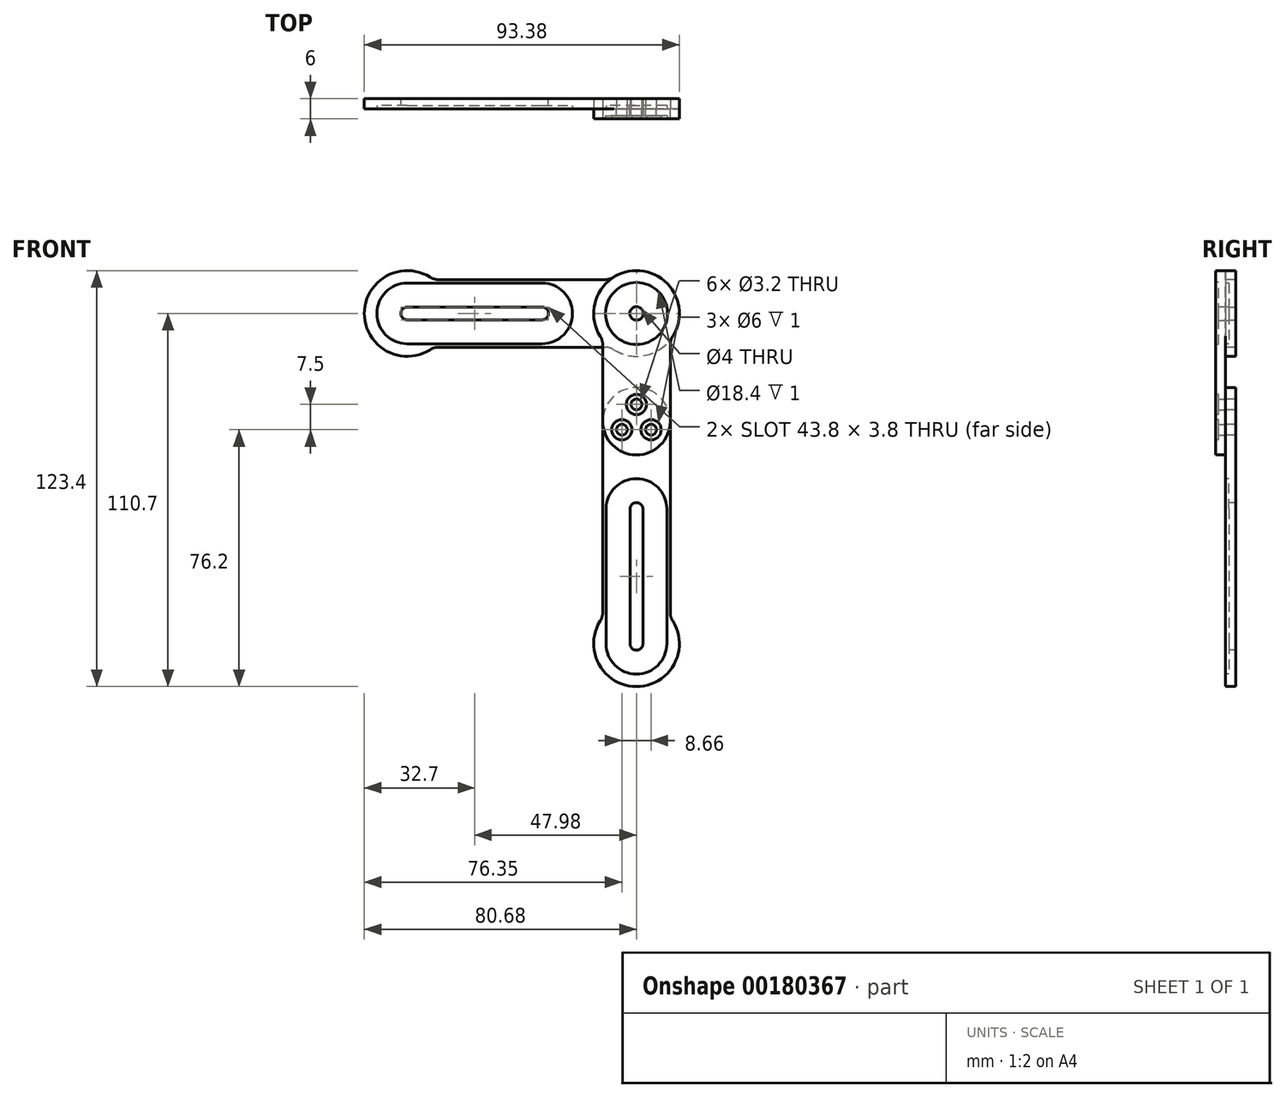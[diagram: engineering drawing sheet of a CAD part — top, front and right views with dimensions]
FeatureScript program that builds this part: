
annotation { "Feature Type Name" : "Feature", "Feature Type Description" : "" }
export const myFeature = defineFeature(function(context is Context, id is Id, definition is map)
    precondition{}
    {
        {
            var Q0;
            Q0=qCreatedBy(makeId("Front.planeOp"),FACE);
            var sketch = newSketch(context, id + "F0", { "sketchPlane" : qUnion([Q0])});
            skLineSegment(sketch, "E0.bottom", {"start": v(0, 0) * mm, "end": v(67.98, 0) * mm, "construction": true});
            skLineSegment(sketch, "E0.top", {"start": v(0, 20) * mm, "end": v(67.98, 20) * mm, "construction": true});
            skLineSegment(sketch, "E0.left", {"start": v(0, 0) * mm, "end": v(0, 20) * mm, "construction": true});
            skLineSegment(sketch, "E0.right", {"start": v(67.98, 0) * mm, "end": v(67.98, 20) * mm, "construction": true});
            skArc(sketch, "E1", {"start": v(0, 0) * mm, "mid": v(-10, 10) * mm, "end": v(0, 20) * mm, "construction": true});
            skArc(sketch, "E2", {"start": v(67.98, 20) * mm, "mid": v(77.98, 10) * mm, "end": v(67.98, 0) * mm, "construction": true});
            skCircle(sketch, "E3", {"center": v(67.98, 10) * mm, "radius": 2 * mm});
            skLineSegment(sketch, "E4", {"start": v(0, 10) * mm, "end": v(20, 10) * mm, "construction": true});
            skLineSegment(sketch, "E5.bottom", {"start": v(0, 11.9) * mm, "end": v(40, 11.9) * mm});
            skLineSegment(sketch, "E5.top", {"start": v(0, 8.1) * mm, "end": v(40, 8.1) * mm});
            skLineSegment(sketch, "E5.left", {"start": v(0, 11.9) * mm, "end": v(0, 8.1) * mm, "construction": true});
            skLineSegment(sketch, "E5.right", {"start": v(40, 11.9) * mm, "end": v(40, 8.1) * mm, "construction": true});
            skPoint(sketch, "E5.middle", {"position": v(20, 10) * mm});
            skArc(sketch, "E6", {"start": v(0, 8.1) * mm, "mid": v(-1.9, 10) * mm, "end": v(0, 11.9) * mm});
            skArc(sketch, "E7", {"start": v(40, 8.1) * mm, "mid": v(41.9, 10) * mm, "end": v(40, 11.9) * mm});
            skCircle(sketch, "E8", {"center": v(67.98, 10) * mm, "radius": 12.7 * mm, "construction": true});
            skCircle(sketch, "E9", {"center": v(0, 10) * mm, "radius": 12.7 * mm, "construction": true});
            skLineSegment(sketch, "E10", {"start": v(60.15, 20) * mm, "end": v(7.83, 20) * mm});
            skLineSegment(sketch, "E11", {"start": v(7.83, 0) * mm, "end": v(60.15, 0) * mm});
            skArc(sketch, "E12", {"start": v(7.83, 20) * mm, "mid": v(-12.7, 10) * mm, "end": v(7.83, 0) * mm});
            skArc(sketch, "E13", {"start": v(60.15, 20) * mm, "mid": v(80.68, 10) * mm, "end": v(60.15, 0) * mm});
            skSolve(sketch);
        }
        {
            var Q0;
            Q0 = qSketchRegion(id + "F0", true);
            extrude(context, id + "F1", {"entities" : qUnion([Q0]), "depth" : 3 * mm, "offsetDistance" : 25 * mm});
        }
        {
            var Q0;
            Q0=makeQuery(id+"F1.opExtrude","CAP_FACE",FACE,{"disambiguationData":[OSD([sQuery(id+"F0.wireOp",EDGE,"E0.bottom"),sQuery(id+"F0.wireOp",EDGE,"E0.top"),sQuery(id+"F0.wireOp",EDGE,"E1"),sQuery(id+"F0.wireOp",EDGE,"E2"),sQuery(id+"F0.wireOp",EDGE,"E3"),sQuery(id+"F0.wireOp",EDGE,"E5.bottom"),sQuery(id+"F0.wireOp",EDGE,"E5.top"),sQuery(id+"F0.wireOp",EDGE,"E6"),sQuery(id+"F0.wireOp",EDGE,"E7")])],"isStart":false});
            var sketch = newSketch(context, id + "F2", { "sketchPlane" : qUnion([Q0])});
            skLineSegment(sketch, "E14", {"start": v(0, 10) * mm, "end": v(40, 10) * mm, "construction": true});
            skLineSegment(sketch, "E15.bottom", {"start": v(40, 19) * mm, "end": v(0, 19) * mm});
            skLineSegment(sketch, "E15.top", {"start": v(40, 1) * mm, "end": v(0, 1) * mm});
            skLineSegment(sketch, "E15.left", {"start": v(40, 19) * mm, "end": v(40, 1) * mm, "construction": true});
            skLineSegment(sketch, "E15.right", {"start": v(0, 19) * mm, "end": v(0, 1) * mm, "construction": true});
            skPoint(sketch, "E15.middle", {"position": v(20, 10) * mm});
            skArc(sketch, "E16", {"start": v(0, 1) * mm, "mid": v(-9, 10) * mm, "end": v(0, 19) * mm});
            skArc(sketch, "E17", {"start": v(40, 19) * mm, "mid": v(49, 10) * mm, "end": v(40, 1) * mm});
            skCircle(sketch, "E18", {"center": v(67.98, 10) * mm, "radius": 9 * mm});
            skSolve(sketch);
        }
        {
            var Q0;
            Q0=makeQuery(id+"F2.imprint","IMPRINT",FACE,{"disambiguationData":[TD([[makeQuery(id+"F2.imprint","IMPRINT",EDGE,{"derivedFrom":sQuery(id+"F2.wireOp",EDGE,"E15.bottom")}),1.0]])]});
            extrude(context, id + "F3", {"entities" : qUnion([Q0]), "operationType" : NewBodyOperationType.REMOVE, "oppositeDirection" : true, "depth" : 1 * mm, "offsetDistance" : 25 * mm});
        }
        {
            var Q0;
            Q0=makeQuery(id+"F1.opExtrude","CAP_FACE",FACE,{"disambiguationData":[OSD([sQuery(id+"F0.wireOp",EDGE,"E0.bottom"),sQuery(id+"F0.wireOp",EDGE,"E0.top"),sQuery(id+"F0.wireOp",EDGE,"E1"),sQuery(id+"F0.wireOp",EDGE,"E2"),sQuery(id+"F0.wireOp",EDGE,"E3"),sQuery(id+"F0.wireOp",EDGE,"E5.bottom"),sQuery(id+"F0.wireOp",EDGE,"E5.top"),sQuery(id+"F0.wireOp",EDGE,"E6"),sQuery(id+"F0.wireOp",EDGE,"E7")])],"isStart":false});
            var sketch = newSketch(context, id + "F4", { "sketchPlane" : qUnion([Q0])});
            skLineSegment(sketch, "E19", {"start": v(67.98, 10) * mm, "end": v(67.98, -22) * mm, "construction": true});
            skLineSegment(sketch, "E20.top", {"start": v(77.98, -22) * mm, "end": v(57.98, -22) * mm, "construction": true});
            skLineSegment(sketch, "E20.left", {"start": v(77.98, 2.17) * mm, "end": v(77.98, -22) * mm});
            skLineSegment(sketch, "E20.right", {"start": v(57.98, 2.17) * mm, "end": v(57.98, -22) * mm});
            skPoint(sketch, "E20.middle", {"position": v(67.98, -6) * mm});
            skPoint(sketch, "E20.cornerSnap0", {"position": v(67.98, 10) * mm});
            skArc(sketch, "E21", {"start": v(77.98, -22) * mm, "mid": v(67.98, -32) * mm, "end": v(57.98, -22) * mm});
            skCircle(sketch, "E22", {"center": v(67.98, 10) * mm, "radius": 2 * mm});
            skCircle(sketch, "E23", {"center": v(67.98, -17) * mm, "radius": 1.6 * mm});
            skCircle(sketch, "E24.1.0", {"center": v(63.65, -24.5) * mm, "radius": 1.6 * mm});
            skCircle(sketch, "E24.2.0", {"center": v(72.31, -24.5) * mm, "radius": 1.6 * mm});
            skCircle(sketch, "E25", {"center": v(67.98, 10) * mm, "radius": 12.7 * mm, "construction": true});
            skArc(sketch, "E26", {"start": v(57.98, 2.17) * mm, "mid": v(67.98, 22.7) * mm, "end": v(77.98, 2.17) * mm});
            skSolve(sketch);
        }
        {
            var Q0;
            Q0 = qSketchRegion(id + "F4", true);
            extrude(context, id + "F5", {"entities" : qUnion([Q0]), "depth" : 3 * mm, "offsetDistance" : 25 * mm});
        }
        {
            var Q0;
            Q0=makeQuery(id+"F5.opExtrude","CAP_FACE",FACE,{"disambiguationData":[OSD([sQuery(id+"F4.wireOp",EDGE,"E20.left"),sQuery(id+"F4.wireOp",EDGE,"E20.right"),sQuery(id+"F4.wireOp",EDGE,"CmDcXUsG-X9iP-GJQO-635Y-WhZAeqbdNLiT"),sQuery(id+"F4.wireOp",EDGE,"E21"),sQuery(id+"F4.wireOp",EDGE,"E22"),sQuery(id+"F4.wireOp",EDGE,"E23"),sQuery(id+"F4.wireOp",EDGE,"E24.1.0"),sQuery(id+"F4.wireOp",EDGE,"E24.2.0")])],"isStart":false});
            var sketch = newSketch(context, id + "F6", { "sketchPlane" : qUnion([Q0])});
            skCircle(sketch, "E27", {"center": v(67.98, -17) * mm, "radius": 3 * mm});
            skCircle(sketch, "E28", {"center": v(63.65, -24.5) * mm, "radius": 3 * mm});
            skCircle(sketch, "E29", {"center": v(72.31, -24.5) * mm, "radius": 3 * mm});
            skCircle(sketch, "E30", {"center": v(67.98, 10) * mm, "radius": 9.2 * mm});
            skSolve(sketch);
        }
        {
            var Q0;
            Q0 = qSketchRegion(id + "F6", true);
            extrude(context, id + "F7", {"entities" : qUnion([Q0]), "operationType" : NewBodyOperationType.REMOVE, "oppositeDirection" : true, "depth" : 1 * mm, "offsetDistance" : 25 * mm});
        }
        {
            var Q0;
            Q0=makeQuery(id+"F5.opExtrude","CAP_FACE",FACE,{"disambiguationData":[OSD([sQuery(id+"F4.wireOp",EDGE,"E20.left"),sQuery(id+"F4.wireOp",EDGE,"E20.right"),sQuery(id+"F4.wireOp",EDGE,"CmDcXUsG-X9iP-GJQO-635Y-WhZAeqbdNLiT"),sQuery(id+"F4.wireOp",EDGE,"E21"),sQuery(id+"F4.wireOp",EDGE,"E22"),sQuery(id+"F4.wireOp",EDGE,"E23"),sQuery(id+"F4.wireOp",EDGE,"E24.1.0"),sQuery(id+"F4.wireOp",EDGE,"E24.2.0")])],"isStart":true});
            var sketch = newSketch(context, id + "F8", { "sketchPlane" : qUnion([Q0])});
            skLineSegment(sketch, "E31", {"start": v(-67.98, -22) * mm, "end": v(-67.98, -88) * mm, "construction": true});
            skLineSegment(sketch, "E32.bottom", {"start": v(-57.98, -22) * mm, "end": v(-77.98, -22) * mm, "construction": true});
            skLineSegment(sketch, "E32.top", {"start": v(-57.98, -88) * mm, "end": v(-77.98, -88) * mm, "construction": true});
            skLineSegment(sketch, "E32.left", {"start": v(-57.98, -22) * mm, "end": v(-57.98, -88) * mm, "construction": true});
            skLineSegment(sketch, "E32.right", {"start": v(-77.98, -22) * mm, "end": v(-77.98, -88) * mm, "construction": true});
            skPoint(sketch, "E32.middle", {"position": v(-67.98, -55) * mm});
            skArc(sketch, "E33", {"start": v(-77.98, -22) * mm, "mid": v(-67.98, -12) * mm, "end": v(-57.98, -22) * mm});
            skArc(sketch, "E34", {"start": v(-57.98, -88) * mm, "mid": v(-67.98, -98) * mm, "end": v(-77.98, -88) * mm, "construction": true});
            skCircle(sketch, "E35.0", {"center": v(-63.65, -24.5) * mm, "radius": 1.6 * mm});
            skCircle(sketch, "E35.1", {"center": v(-67.98, -17) * mm, "radius": 1.6 * mm});
            skCircle(sketch, "E35.2", {"center": v(-72.31, -24.5) * mm, "radius": 1.6 * mm});
            skLineSegment(sketch, "E36", {"start": v(-67.98, -88) * mm, "end": v(-67.98, -68) * mm, "construction": true});
            skLineSegment(sketch, "E37.bottom", {"start": v(-66.08, -88) * mm, "end": v(-69.88, -88) * mm, "construction": true});
            skLineSegment(sketch, "E37.top", {"start": v(-66.08, -48) * mm, "end": v(-69.88, -48) * mm, "construction": true});
            skLineSegment(sketch, "E37.left", {"start": v(-66.08, -88) * mm, "end": v(-66.08, -48) * mm});
            skLineSegment(sketch, "E37.right", {"start": v(-69.88, -88) * mm, "end": v(-69.88, -48) * mm});
            skPoint(sketch, "E37.middle", {"position": v(-67.98, -68) * mm});
            skArc(sketch, "E38", {"start": v(-66.08, -88) * mm, "mid": v(-67.98, -89.9) * mm, "end": v(-69.88, -88) * mm});
            skArc(sketch, "E39", {"start": v(-66.08, -48) * mm, "mid": v(-67.98, -46.1) * mm, "end": v(-69.88, -48) * mm});
            skCircle(sketch, "E40", {"center": v(-67.98, -88) * mm, "radius": 12.7 * mm, "construction": true});
            skLineSegment(sketch, "E41", {"start": v(-77.98, -22) * mm, "end": v(-77.98, -80.17) * mm});
            skLineSegment(sketch, "E42", {"start": v(-57.98, -22) * mm, "end": v(-57.98, -80.17) * mm});
            skArc(sketch, "E43", {"start": v(-57.98, -80.17) * mm, "mid": v(-67.98, -100.7) * mm, "end": v(-77.98, -80.17) * mm});
            skSolve(sketch);
        }
        {
            var Q0;
            Q0 = qSketchRegion(id + "F8", true);
            extrude(context, id + "F9", {"entities" : qUnion([Q0]), "depth" : 3 * mm, "offsetDistance" : 25 * mm});
        }
        {
            var Q0;
            Q0=makeQuery(id+"F9.opExtrude","CAP_FACE",FACE,{"disambiguationData":[OSD([sQuery(id+"F8.wireOp",EDGE,"E32.left"),sQuery(id+"F8.wireOp",EDGE,"E32.right"),sQuery(id+"F8.wireOp",EDGE,"E33"),sQuery(id+"F8.wireOp",EDGE,"E34"),sQuery(id+"F8.wireOp",EDGE,"E35.0"),sQuery(id+"F8.wireOp",EDGE,"E35.1"),sQuery(id+"F8.wireOp",EDGE,"E35.2"),sQuery(id+"F8.wireOp",EDGE,"E37.left"),sQuery(id+"F8.wireOp",EDGE,"E37.right"),sQuery(id+"F8.wireOp",EDGE,"E38"),sQuery(id+"F8.wireOp",EDGE,"E39")])],"isStart":true});
            var sketch = newSketch(context, id + "F10", { "sketchPlane" : qUnion([Q0])});
            skLineSegment(sketch, "E44", {"start": v(67.98, -88) * mm, "end": v(67.98, -48) * mm, "construction": true});
            skLineSegment(sketch, "E45.bottom", {"start": v(76.98, -48) * mm, "end": v(58.98, -48) * mm, "construction": true});
            skLineSegment(sketch, "E45.top", {"start": v(76.98, -88) * mm, "end": v(58.98, -88) * mm, "construction": true});
            skLineSegment(sketch, "E45.left", {"start": v(76.98, -48) * mm, "end": v(76.98, -88) * mm});
            skLineSegment(sketch, "E45.right", {"start": v(58.98, -48) * mm, "end": v(58.98, -88) * mm});
            skPoint(sketch, "E45.middle", {"position": v(67.98, -68) * mm});
            skArc(sketch, "E46", {"start": v(58.98, -48) * mm, "mid": v(67.98, -39) * mm, "end": v(76.98, -48) * mm});
            skArc(sketch, "E47", {"start": v(76.98, -88) * mm, "mid": v(67.98, -97) * mm, "end": v(58.98, -88) * mm});
            skLineSegment(sketch, "E48", {"start": v(69.88, -88) * mm, "end": v(66.08, -88) * mm, "construction": true});
            skSolve(sketch);
        }
        {
            var Q0;
            Q0 = qSketchRegion(id + "F10", true);
            extrude(context, id + "F11", {"entities" : qUnion([Q0]), "operationType" : NewBodyOperationType.REMOVE, "oppositeDirection" : true, "depth" : 1 * mm, "offsetDistance" : 25 * mm});
        }
        {
            var Q0;
            Q0=makeQuery(id+"F1.opExtrude","SWEPT_EDGE",EDGE,{"disambiguationData":[OSD([sQuery(id+"F0.wireOp",EDGE,"E10"),sQuery(id+"F0.wireOp",EDGE,"E12")])]});
            var Q1;
            Q1=makeQuery(id+"F1.opExtrude","SWEPT_EDGE",EDGE,{"disambiguationData":[OSD([sQuery(id+"F0.wireOp",EDGE,"E11"),sQuery(id+"F0.wireOp",EDGE,"E12")])]});
            var Q2;
            Q2=makeQuery(id+"F1.opExtrude","SWEPT_EDGE",EDGE,{"disambiguationData":[OSD([sQuery(id+"F0.wireOp",EDGE,"E11"),sQuery(id+"F0.wireOp",EDGE,"E13")])]});
            var Q3;
            Q3=makeQuery(id+"F1.opExtrude","SWEPT_EDGE",EDGE,{"disambiguationData":[OSD([sQuery(id+"F0.wireOp",EDGE,"E10"),sQuery(id+"F0.wireOp",EDGE,"E13")])]});
            var Q4;
            Q4=makeQuery(id+"F5.opExtrude","SWEPT_EDGE",EDGE,{"disambiguationData":[OSD([sQuery(id+"F4.wireOp",EDGE,"E20.right"),sQuery(id+"F4.wireOp",EDGE,"E26")])]});
            var Q5;
            Q5=makeQuery(id+"F5.opExtrude","SWEPT_EDGE",EDGE,{"disambiguationData":[OSD([sQuery(id+"F0.wireOp",EDGE,"E13"),sQuery(id+"F4.wireOp",EDGE,"E20.left"),sQuery(id+"F4.wireOp",EDGE,"E26")])]});
            var Q6;
            Q6=makeQuery(id+"F9.opExtrude","SWEPT_EDGE",EDGE,{"disambiguationData":[OSD([sQuery(id+"F8.wireOp",EDGE,"E41"),sQuery(id+"F8.wireOp",EDGE,"E43")])]});
            var Q7;
            Q7=makeQuery(id+"F9.opExtrude","SWEPT_EDGE",EDGE,{"disambiguationData":[OSD([sQuery(id+"F8.wireOp",EDGE,"E42"),sQuery(id+"F8.wireOp",EDGE,"E43")])]});
            fillet(context, id + "F12", {"entities" : qUnion([Q0, Q1, Q2, Q3, Q4, Q5, Q6, Q7]), "radius" : 5 * mm, "tangentPropagation" : true, "allowEdgeOverflow" : false});
        }
        {
            var Q0;
            Q0=makeQuery(id+"F1.opExtrude","CAP_FACE",FACE,{"disambiguationData":[OSD([sQuery(id+"F0.wireOp",EDGE,"E3"),sQuery(id+"F0.wireOp",EDGE,"E5.bottom"),sQuery(id+"F0.wireOp",EDGE,"E5.top"),sQuery(id+"F0.wireOp",EDGE,"E6"),sQuery(id+"F0.wireOp",EDGE,"E7"),sQuery(id+"F0.wireOp",EDGE,"E10"),sQuery(id+"F0.wireOp",EDGE,"E11"),sQuery(id+"F0.wireOp",EDGE,"E12"),sQuery(id+"F0.wireOp",EDGE,"E13")])],"isStart":false});
            var sketch = newSketch(context, id + "F13", { "sketchPlane" : qUnion([Q0])});
            skCircle(sketch, "E49", {"center": v(67.98, 10) * mm, "radius": 4.5 * mm, "construction": true});
            skCircle(sketch, "E50", {"center": v(67.98, 10) * mm, "radius": 8.5 * mm, "construction": true});
            skCircle(sketch, "E51", {"center": v(67.98, 18.5) * mm, "radius": 1.25 * mm});
            skLineSegment(sketch, "E52", {"start": v(67.98, 10) * mm, "end": v(67.98, 18.5) * mm, "construction": true});
            skCircle(sketch, "E53.1.0", {"center": v(63.73, 17.36) * mm, "radius": 1.25 * mm});
            skCircle(sketch, "E53.2.0", {"center": v(60.62, 14.25) * mm, "radius": 1.25 * mm});
            skCircle(sketch, "E53.3.0", {"center": v(59.48, 10) * mm, "radius": 1.25 * mm});
            skCircle(sketch, "E53.4.0", {"center": v(60.62, 5.75) * mm, "radius": 1.25 * mm});
            skCircle(sketch, "E53.5.0", {"center": v(63.73, 2.64) * mm, "radius": 1.25 * mm});
            skCircle(sketch, "E53.6.0", {"center": v(67.98, 1.5) * mm, "radius": 1.25 * mm});
            skCircle(sketch, "E53.7.0", {"center": v(72.23, 2.64) * mm, "radius": 1.25 * mm});
            skCircle(sketch, "E53.8.0", {"center": v(75.34, 5.75) * mm, "radius": 1.25 * mm});
            skCircle(sketch, "E53.9.0", {"center": v(76.48, 10) * mm, "radius": 1.25 * mm});
            skCircle(sketch, "E53.10.0", {"center": v(75.34, 14.25) * mm, "radius": 1.25 * mm});
            skCircle(sketch, "E53.11.0", {"center": v(72.23, 17.36) * mm, "radius": 1.25 * mm});
            skLineSegment(sketch, "E54", {"start": v(67.98, 10) * mm, "end": v(72.23, 17.36) * mm, "construction": true});
            skLineSegment(sketch, "E55", {"start": v(72.23, 17.36) * mm, "end": v(67.98, 18.5) * mm, "construction": true});
            skLineSegment(sketch, "E56", {"start": v(67.98, 10) * mm, "end": v(70.1, 17.93) * mm, "construction": true});
            skCircle(sketch, "E57", {"center": v(69.14, 14.35) * mm, "radius": 0.75 * mm});
            skCircle(sketch, "E58.1.0", {"center": v(66.82, 14.35) * mm, "radius": 0.75 * mm});
            skCircle(sketch, "E58.2.0", {"center": v(64.8, 13.18) * mm, "radius": 0.75 * mm});
            skCircle(sketch, "E58.3.0", {"center": v(63.63, 11.16) * mm, "radius": 0.75 * mm});
            skCircle(sketch, "E58.4.0", {"center": v(63.63, 8.84) * mm, "radius": 0.75 * mm});
            skCircle(sketch, "E58.5.0", {"center": v(64.8, 6.82) * mm, "radius": 0.75 * mm});
            skCircle(sketch, "E58.6.0", {"center": v(66.82, 5.65) * mm, "radius": 0.75 * mm});
            skCircle(sketch, "E58.7.0", {"center": v(69.14, 5.65) * mm, "radius": 0.75 * mm});
            skCircle(sketch, "E58.8.0", {"center": v(71.16, 6.82) * mm, "radius": 0.75 * mm});
            skCircle(sketch, "E58.9.0", {"center": v(72.33, 8.84) * mm, "radius": 0.75 * mm});
            skCircle(sketch, "E58.10.0", {"center": v(72.33, 11.16) * mm, "radius": 0.75 * mm});
            skCircle(sketch, "E58.11.0", {"center": v(71.16, 13.18) * mm, "radius": 0.75 * mm});
            skSolve(sketch);
        }
        {
            var Q0;
            Q0 = qSketchRegion(id + "F13", true);
            extrude(context, id + "F14", {"entities" : qUnion([Q0]), "operationType" : NewBodyOperationType.ADD, "depth" : 0.5 * mm, "offsetDistance" : 25 * mm});
        }
    });
